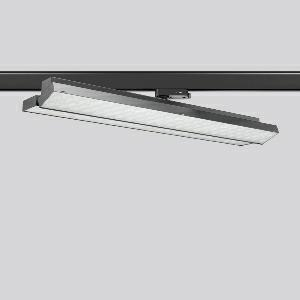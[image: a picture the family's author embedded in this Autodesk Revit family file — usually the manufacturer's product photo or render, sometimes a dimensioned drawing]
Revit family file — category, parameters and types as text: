
# Revit family: tx-move_742162_003_76_5bb8
name_source: partatom
category: Lighting Fixtures
units: mm (PartAtom-declared; Revit-internal decimal feet)

## family parameters
Cut with Voids When Loaded = No
Host = Face
Light Source = No
Part Type = Normal
Room Calculation Point = No
Round Connector Dimension = Use Diameter
Shared = No

## types (1)
- MultiLumen 1 (1 x LED Modul 830, 2925 lm, 3000)
    Apparent Load = 41 VA
    CIE Flux Codes = 77 96 99 100 100
    Color Rendering = 80
    Color Temperature = 3000
    Default Elevation = 1800 mm
    Description = Series: TX-MOVE
Multifunctional surface-mounted spotlight for area lighting. Very flat design. Housing: sheet steel, powder-coated. Rotation range: 356°. Swivel range: 90°. Consistent alignment possible with visible tilt scale. High-efficiency LED units with optimum light control thanks to clear plastic (PC) lens optics. Spezielle Mikrostrukturen reduzieren Gelbsaum. Symmetrical light distribution. With adapter for RZB 3-circuit DALI tracks. Suitable for Track on ceiling. MultiLumen: Luminous flux adjustable in 3 steps. Factory setting is the highest luminous flux. Environmentally friendly and resource-saving due to replaceable and recyclable components. 
Colour: deep black, matt (RAL 9005)
Length: 570 mm
Width: 119 mm
Height: 88 mm
Lamp: LED
Socket: without socket
Colour temperature: 3000K
Colour rendering index (CRI): 80
System power: 41 W
Rated luminous flux: 5850 lm
Luminous efficiency: 143 lm/W
System power 2: 57 W
Rated luminous flux 2: 7950 lm
Luminous efficiency 2: 139 lm/W
System power 3: 73 W
Rated luminous flux 3: 9700 lm
Luminous efficiency 3: 133 lm/W
Control gear: Dimmable EVG, DALI
Protection class: I
Type of protection: IP 20
    Height = 75 mm
    Lamp = 1 x LED Modul 830
    Lamp Light Flux = 2925 lm
    Lamp count = 1
    Length = 569 mm
    Lifetime = 50000 h
    Luminous efficacy = 143 lm/W
    Manufacturer = RZB
    ModVariant = No
    Model = 742162.003.76
    Mounting Place = Ceiling
    Mounting Type = Surface mounted
    Number of Poles = 1
    OnlyDefault = Yes
    Power Factor = 1
    Product Name = TX-MOVE
    Product group = Track mounted projectors
    ProductGroupID = 301
    Protection Class = Protection class I
    Protection Degree = IP 20
    RLX_Detail_Level = 1
    RLX_Emergency_Light_Flux = 0 lm
    RLX_Emergency_Type = 0
    RLX_Emergency_Type_DB = No
    RlxData = <blob elided: 36629 chars, md5=87747130>
    Socket = socket
    Standby Power = 0 W
    System Light Flux = 5850 lm
    System Power = 41 W
    Type Comments = MultiLumen 1
    Type Image = 742162.003.jpg
    URL = http://relux.com
    VarID = multilumen_1
    Voltage = 0 V
    Weight = 0.00 kg
    Width = 119 mm

## geometry (parser evidence)
native form markers: Blend x4, Sweep x13
no freeform markers — native parametric forms only
